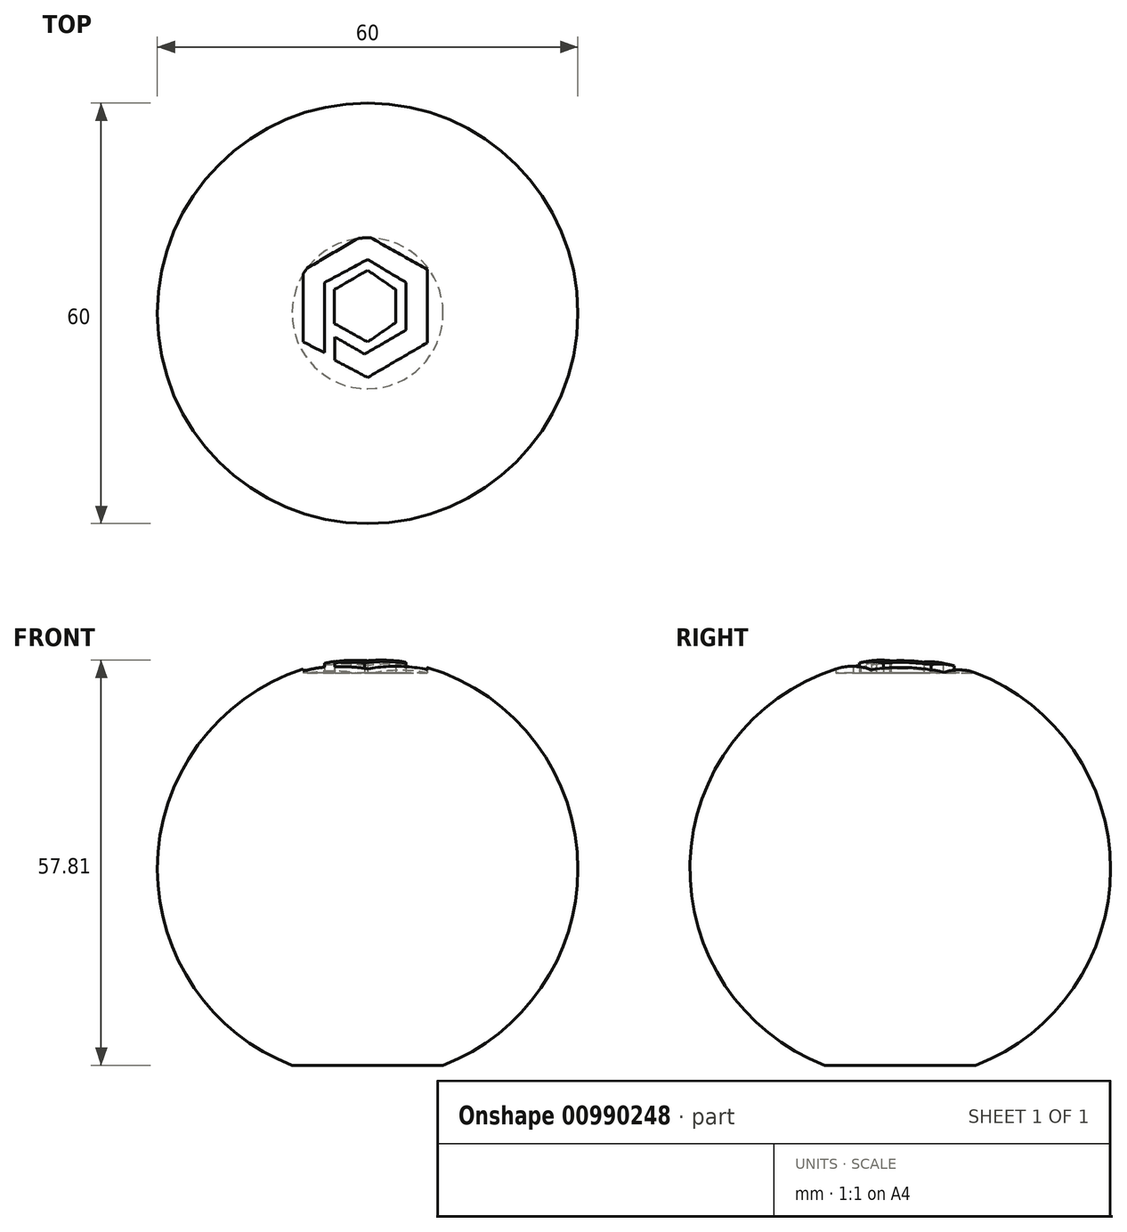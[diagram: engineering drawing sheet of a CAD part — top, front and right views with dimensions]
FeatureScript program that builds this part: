
annotation { "Feature Type Name" : "Feature", "Feature Type Description" : "" }
export const myFeature = defineFeature(function(context is Context, id is Id, definition is map)
    precondition{}
    {
        {
            assignVariable(context, id + "F0", {"name" : "diameter", "anyValue" : 60});
        }
        {
            var Q0;
            Q0=qCreatedBy(makeId("Front.planeOp"),FACE);
            var sketch = newSketch(context, id + "F1", { "sketchPlane" : qUnion([Q0])});
            skArc(sketch, "E0", {"start": v(30, 0) * mm, "mid": v(0, 30) * mm, "end": v(-30, 0) * mm});
            skLineSegment(sketch, "E1", {"start": v(-30, 0) * mm, "end": v(30, 0) * mm});
            skSolve(sketch);
        }
        {
            var Q0;
            Q0 = qSketchRegion(id + "F1", true);
            var Q1;
            Q1=sQuery(id+"F1.wireOp",EDGE,"E1");
            revolve(context, id + "F2", {"surfaceOperationType" : NewSurfaceOperationType.NEW, "entities" : qUnion([Q0]), "axis" : qUnion([Q1]), "revolveType" : RevolveType.FULL});
        }
        {
            var Q0;
            Q0=qCreatedBy(makeId("Top.planeOp"),FACE);
            var sketch = newSketch(context, id + "F3", { "sketchPlane" : qUnion([Q0])});
            skLineSegment(sketch, "E2", {"start": v(-9.17, -4.1) * mm, "end": v(-9.17, 6.13) * mm});
            skLineSegment(sketch, "E3", {"start": v(-9.17, 6.13) * mm, "end": v(-0.42, 11.26) * mm});
            skLineSegment(sketch, "E4", {"start": v(-0.42, 11.26) * mm, "end": v(8.54, 6.24) * mm});
            skLineSegment(sketch, "E5", {"start": v(8.54, 6.24) * mm, "end": v(8.54, -4.2) * mm});
            skLineSegment(sketch, "E6", {"start": v(8.54, -4.2) * mm, "end": v(0, -9.16) * mm});
            skLineSegment(sketch, "E7", {"start": v(0, -9.16) * mm, "end": v(-4.67, -6.7) * mm});
            skLineSegment(sketch, "E8", {"start": v(-4.67, -6.7) * mm, "end": v(-4.67, -3.38) * mm});
            skLineSegment(sketch, "E9", {"start": v(-4.67, -3.38) * mm, "end": v(-0.43, -5.82) * mm});
            skLineSegment(sketch, "E10", {"start": v(-0.43, -5.82) * mm, "end": v(5.5, -2.38) * mm});
            skLineSegment(sketch, "E11", {"start": v(5.5, -2.38) * mm, "end": v(5.5, 4.38) * mm});
            skLineSegment(sketch, "E12", {"start": v(5.5, 4.38) * mm, "end": v(0, 7.68) * mm});
            skLineSegment(sketch, "E13", {"start": v(0, 7.68) * mm, "end": v(-6.13, 4.38) * mm});
            skLineSegment(sketch, "E14", {"start": v(-6.13, 4.38) * mm, "end": v(-6.13, -5.62) * mm});
            skLineSegment(sketch, "E15", {"start": v(-6.13, -5.62) * mm, "end": v(-9.17, -4.1) * mm});
            skLineSegment(sketch, "E16", {"start": v(-4.72, -1.47) * mm, "end": v(-4.72, 3.39) * mm});
            skLineSegment(sketch, "E17", {"start": v(-4.72, 3.39) * mm, "end": v(0, 6.14) * mm});
            skLineSegment(sketch, "E18", {"start": v(0, 6.14) * mm, "end": v(4, 3.39) * mm});
            skLineSegment(sketch, "E19", {"start": v(4, 3.39) * mm, "end": v(4, -1.33) * mm});
            skLineSegment(sketch, "E20", {"start": v(4, -1.33) * mm, "end": v(0, -4.1) * mm});
            skLineSegment(sketch, "E21", {"start": v(0, -4.1) * mm, "end": v(-4.72, -1.47) * mm});
            skSolve(sketch);
        }
        {
            var Q0;
            Q0 = qSketchRegion(id + "F3", true);
            extrude(context, id + "F4", {"entities" : qUnion([Q0]), "operationType" : NewBodyOperationType.REMOVE, "depth" : 50 * mm, "offsetDistance" : 25 * mm, "hasSecondDirection" : true, "secondDirectionOppositeDirection" : false, "secondDirectionDepth" : ((getVariable(context, 'diameter') / 2) - 2) * mm});
        }
        {
            var Q0;
            Q0=qCreatedBy(makeId("Top.planeOp"),FACE);
            var sketch = newSketch(context, id + "F5", { "sketchPlane" : qUnion([Q0])});
            skLineSegment(sketch, "E22.bottom", {"start": v(-28.02, 29.4) * mm, "end": v(31.98, 29.4) * mm});
            skLineSegment(sketch, "E22.top", {"start": v(-28.02, -30.6) * mm, "end": v(31.98, -30.6) * mm});
            skLineSegment(sketch, "E22.left", {"start": v(-28.02, 29.4) * mm, "end": v(-28.02, -30.6) * mm});
            skLineSegment(sketch, "E22.right", {"start": v(31.98, 29.4) * mm, "end": v(31.98, -30.6) * mm});
            skSolve(sketch);
        }
        {
            var Q0;
            Q0 = qSketchRegion(id + "F5", true);
            extrude(context, id + "F6", {"entities" : qUnion([Q0]), "operationType" : NewBodyOperationType.REMOVE, "oppositeDirection" : true, "depth" : 100 * mm, "offsetDistance" : 25 * mm, "hasSecondDirection" : true, "secondDirectionOppositeDirection" : true, "secondDirectionDepth" : ((getVariable(context, 'diameter') / 2) - 2) * mm});
        }
    });
